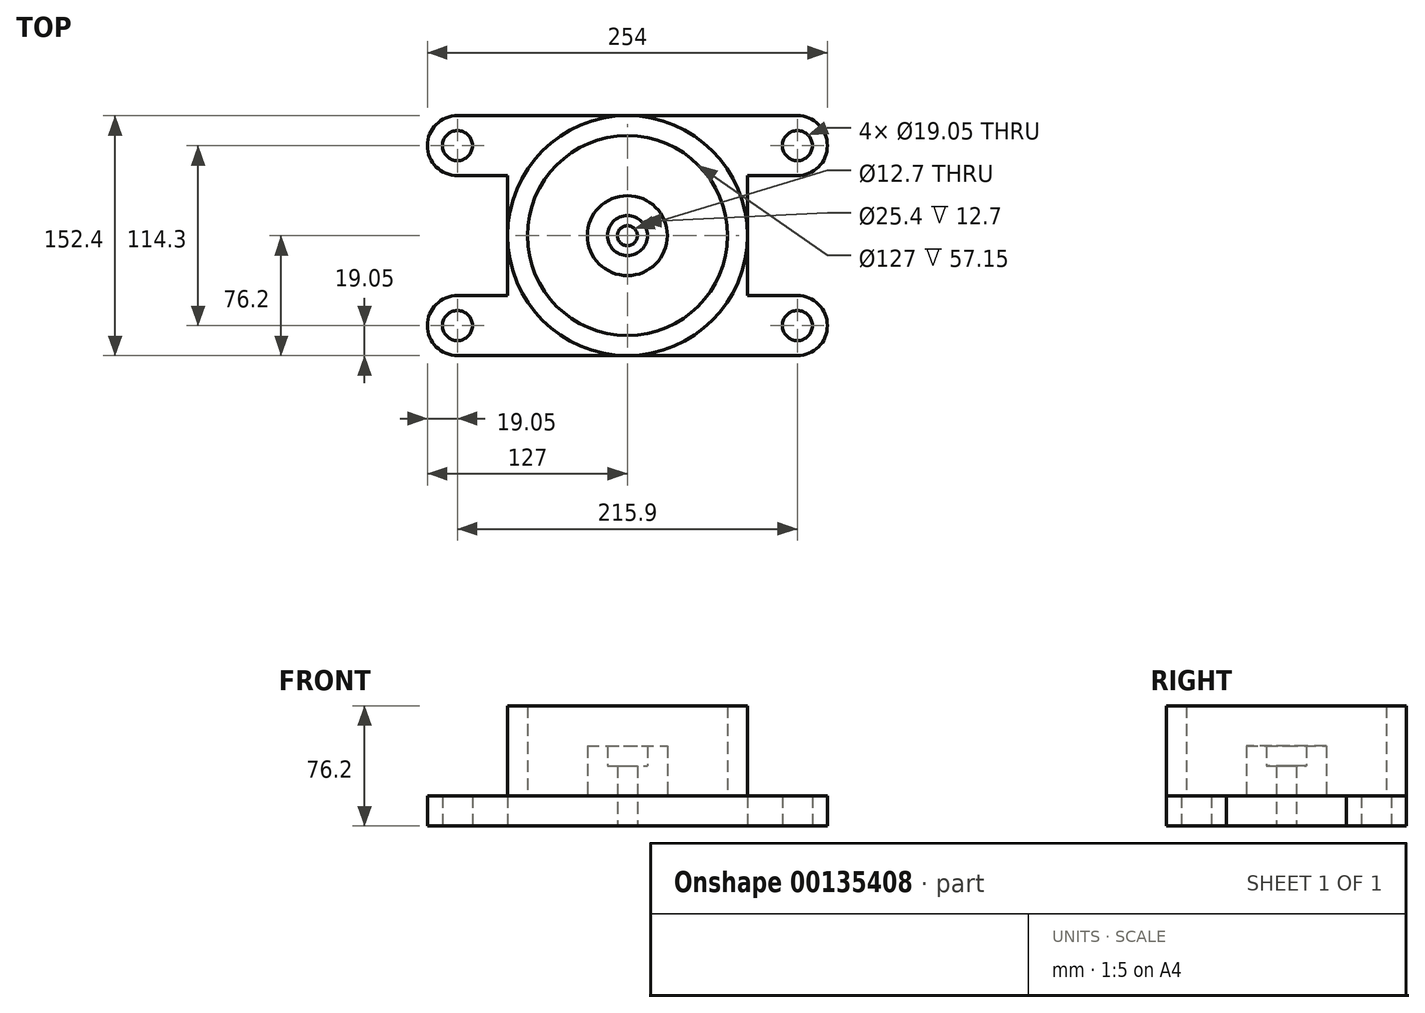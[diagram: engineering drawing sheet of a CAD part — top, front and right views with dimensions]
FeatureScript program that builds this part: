
annotation { "Feature Type Name" : "Feature", "Feature Type Description" : "" }
export const myFeature = defineFeature(function(context is Context, id is Id, definition is map)
    precondition{}
    {
        {
            var Q0;
            Q0=qCreatedBy(makeId("Front.planeOp"),FACE);
            var sketch = newSketch(context, id + "F0", { "sketchPlane" : qUnion([Q0])});
            skLineSegment(sketch, "E0", {"start": v(-6.35, 0) * mm, "end": v(-76.2, 0) * mm});
            skLineSegment(sketch, "E1", {"start": v(-76.2, 0) * mm, "end": v(-76.2, 76.2) * mm});
            skLineSegment(sketch, "E2", {"start": v(-76.2, 76.2) * mm, "end": v(-63.5, 76.2) * mm});
            skLineSegment(sketch, "E3", {"start": v(-63.5, 76.2) * mm, "end": v(-63.5, 19.05) * mm});
            skLineSegment(sketch, "E4", {"start": v(-63.5, 19.05) * mm, "end": v(-25.4, 19.05) * mm});
            skLineSegment(sketch, "E5", {"start": v(-25.4, 19.05) * mm, "end": v(-25.4, 50.8) * mm});
            skLineSegment(sketch, "E6", {"start": v(-25.4, 50.8) * mm, "end": v(-12.7, 50.8) * mm});
            skLineSegment(sketch, "E7", {"start": v(-12.7, 50.8) * mm, "end": v(-12.7, 38.1) * mm});
            skLineSegment(sketch, "E8", {"start": v(-12.7, 38.1) * mm, "end": v(-6.35, 38.1) * mm});
            skLineSegment(sketch, "E9", {"start": v(-6.35, 38.1) * mm, "end": v(-6.35, 0) * mm});
            skLineSegment(sketch, "E10", {"start": v(0, 0) * mm, "end": v(0, 76.2) * mm});
            skSolve(sketch);
        }
        {
            var Q0;
            Q0=makeQuery(id+"F0.imprint","IMPRINT",FACE,{"disambiguationData":[TD([[makeQuery(id+"F0.imprint","IMPRINT",EDGE,{"derivedFrom":sQuery(id+"F0.wireOp",EDGE,"E0")}),-1.0]])]});
            var Q1;
            Q1=sQuery(id+"F0.wireOp",EDGE,"E10");
            revolve(context, id + "F1", {"entities" : qUnion([Q0]), "axis" : qUnion([Q1]), "revolveType" : RevolveType.FULL});
        }
        {
            var Q0;
            Q0=qCreatedBy(makeId("Top.planeOp"),FACE);
            var sketch = newSketch(context, id + "F2", { "sketchPlane" : qUnion([Q0])});
            skLineSegment(sketch, "E11", {"start": v(0, -76.2) * mm, "end": v(-107.95, -76.2) * mm});
            skLineSegment(sketch, "E12", {"start": v(-107.95, -76.2) * mm, "end": v(-107.95, -66.68) * mm});
            skLineSegment(sketch, "E13", {"start": v(-107.95, -38.1) * mm, "end": v(-76.2, -38.1) * mm});
            skLineSegment(sketch, "E14", {"start": v(-76.2, -38.1) * mm, "end": v(-76.2, 0) * mm});
            skArc(sketch, "E15", {"start": v(-107.95, -38.1) * mm, "mid": v(-127, -57.15) * mm, "end": v(-107.95, -76.2) * mm});
            skCircle(sketch, "E16", {"center": v(-107.95, -57.15) * mm, "radius": 9.53 * mm});
            skLineSegment(sketch, "E17.trimOffspring", {"start": v(-107.95, -47.63) * mm, "end": v(-107.95, -38.1) * mm});
            skArc(sketch, "E18.0", {"start": v(-76.2, 0) * mm, "mid": v(-53.88, -53.88) * mm, "end": v(0, -76.2) * mm});
            skLineSegment(sketch, "E19.MirrorCS", {"start": v(0, 76.2) * mm, "end": v(-107.95, 76.2) * mm});
            skArc(sketch, "E20.MirrorCS", {"start": v(-107.95, 38.1) * mm, "mid": v(-127, 57.15) * mm, "end": v(-107.95, 76.2) * mm});
            skCircle(sketch, "E21.MirrorC", {"center": v(-107.95, 57.15) * mm, "radius": 9.53 * mm});
            skLineSegment(sketch, "E22.MirrorCS", {"start": v(-107.95, 38.1) * mm, "end": v(-76.2, 38.1) * mm});
            skLineSegment(sketch, "E23.MirrorCS", {"start": v(-76.2, 38.1) * mm, "end": v(-76.2, 0) * mm});
            skArc(sketch, "E24.MirrorCS", {"start": v(-76.2, 0) * mm, "mid": v(-53.88, 53.88) * mm, "end": v(0, 76.2) * mm});
            skLineSegment(sketch, "E25.MirrorCS", {"start": v(107.95, 38.1) * mm, "end": v(76.2, 38.1) * mm});
            skArc(sketch, "E26.MirrorCS", {"start": v(107.95, 38.1) * mm, "mid": v(127, 57.15) * mm, "end": v(107.95, 76.2) * mm});
            skLineSegment(sketch, "E27.MirrorCS", {"start": v(0, 76.2) * mm, "end": v(107.95, 76.2) * mm});
            skLineSegment(sketch, "E28.MirrorCS", {"start": v(76.2, 38.1) * mm, "end": v(76.2, 0) * mm});
            skArc(sketch, "E29.MirrorCS", {"start": v(76.2, 0) * mm, "mid": v(53.88, 53.88) * mm, "end": v(0, 76.2) * mm});
            skLineSegment(sketch, "E30.MirrorCS", {"start": v(76.2, -38.1) * mm, "end": v(76.2, 0) * mm});
            skLineSegment(sketch, "E31.MirrorCS", {"start": v(107.95, -38.1) * mm, "end": v(76.2, -38.1) * mm});
            skArc(sketch, "E32.MirrorCS", {"start": v(107.95, -38.1) * mm, "mid": v(127, -57.15) * mm, "end": v(107.95, -76.2) * mm});
            skCircle(sketch, "E33.MirrorC", {"center": v(107.95, 57.15) * mm, "radius": 9.53 * mm});
            skCircle(sketch, "E34.MirrorC", {"center": v(107.95, -57.15) * mm, "radius": 9.53 * mm});
            skLineSegment(sketch, "E35.MirrorCS", {"start": v(0, -76.2) * mm, "end": v(107.95, -76.2) * mm});
            skArc(sketch, "E36.MirrorCS", {"start": v(76.2, 0) * mm, "mid": v(53.88, -53.88) * mm, "end": v(0, -76.2) * mm});
            skSolve(sketch);
        }
        {
            var Q0;
            Q0=makeQuery(id+"F2.imprint","IMPRINT",FACE,{"disambiguationData":[TD([[makeQuery(id+"F2.imprint","IMPRINT",EDGE,{"derivedFrom":sQuery(id+"F2.wireOp",EDGE,"E11")}),-1.0]])]});
            var Q1;
            {var subQ0=sQuery(id+"F2.wireOp",EDGE,"E12");Q1=makeQuery(id+"F2.imprint","IMPRINT",FACE,{"disambiguationData":[TD([[makeQuery(id+"F2.imprint","IMPRINT",EDGE,{"derivedFrom":subQ0}),1.0]])]});}
            var Q2;
            Q2=makeQuery(id+"F2.imprint","IMPRINT",FACE,{"disambiguationData":[TD([[makeQuery(id+"F2.imprint","IMPRINT",EDGE,{"derivedFrom":sQuery(id+"F2.wireOp",EDGE,"E19.MirrorCS")}),1.0]])]});
            var Q3;
            Q3=makeQuery(id+"F2.imprint","IMPRINT",FACE,{"disambiguationData":[TD([[makeQuery(id+"F2.imprint","IMPRINT",EDGE,{"derivedFrom":sQuery(id+"F2.wireOp",EDGE,"E25.MirrorCS")}),-1.0]])]});
            var Q4;
            Q4=makeQuery(id+"F2.imprint","IMPRINT",FACE,{"disambiguationData":[TD([[makeQuery(id+"F2.imprint","IMPRINT",EDGE,{"derivedFrom":sQuery(id+"F2.wireOp",EDGE,"E30.MirrorCS")}),1.0]])]});
            extrude(context, id + "F3", {"entities" : qUnion([Q0, Q1, Q2, Q3, Q4]), "operationType" : NewBodyOperationType.ADD, "depth" : 19.05 * mm});
        }
    });
